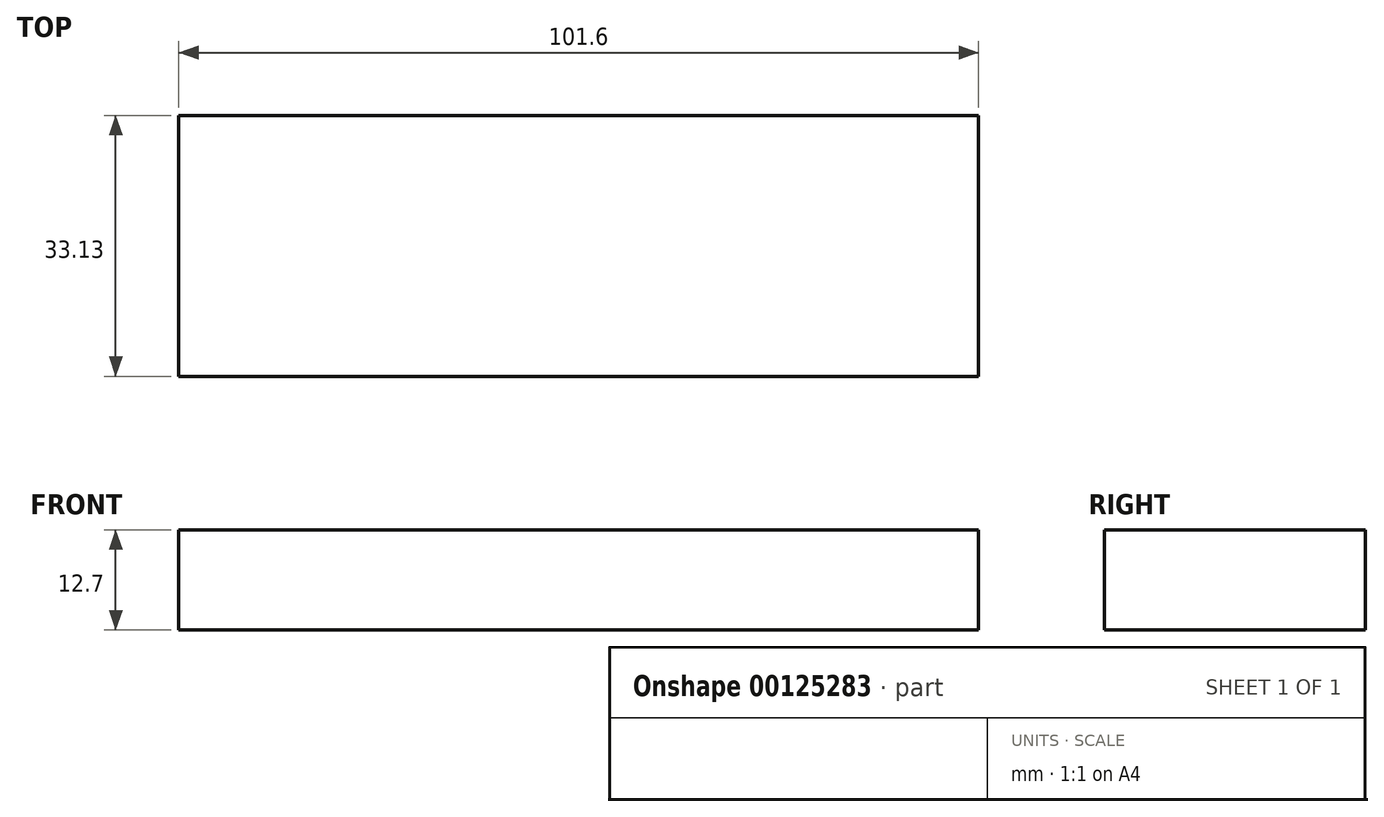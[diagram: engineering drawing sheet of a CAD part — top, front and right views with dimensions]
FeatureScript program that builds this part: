
annotation { "Feature Type Name" : "Feature", "Feature Type Description" : "" }
export const myFeature = defineFeature(function(context is Context, id is Id, definition is map)
    precondition{}
    {
        {
            var Q0;
            Q0=qCreatedBy(makeId("Top.planeOp"),FACE);
            var sketch = newSketch(context, id + "F0", { "sketchPlane" : qUnion([Q0])});
            skLineSegment(sketch, "E0.bottom", {"start": v(0, 0) * mm, "end": v(101.6, 0) * mm});
            skLineSegment(sketch, "E0.top", {"start": v(0, 33.13) * mm, "end": v(101.6, 33.13) * mm});
            skLineSegment(sketch, "E0.left", {"start": v(0, 0) * mm, "end": v(0, 33.13) * mm});
            skLineSegment(sketch, "E0.right", {"start": v(101.6, 0) * mm, "end": v(101.6, 33.13) * mm});
            skSolve(sketch);
        }
        {
            var Q0;
            Q0=makeQuery(id+"F0.imprint","IMPRINT",FACE,{"disambiguationData":[TD([[makeQuery(id+"F0.imprint","IMPRINT",EDGE,{"derivedFrom":sQuery(id+"F0.wireOp",EDGE,"E0.bottom")}),1.0]])]});
            extrude(context, id + "F1", {"entities" : qUnion([Q0]), "depth" : 12.7 * mm});
        }
    });
